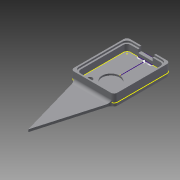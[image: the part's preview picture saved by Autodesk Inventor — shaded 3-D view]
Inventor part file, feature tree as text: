
AUTODESK INVENTOR PART (.ipt)
format: ipt  version: 2015 SP1 (Build 190203100, 203)  size: 185,856 bytes
history: native  units: mm
features: sketch x7, extrude x5, fillet x4, other x2, projected_geometry x1, reference x1
ambient origin geometry x8: Origin, YZ Plane, XZ Plane, XY Plane, X Axis, Y Axis, Z Axis, Center Point
bodies: Body1 (feature_tree)
feature tree (20):
  other  "Sólido1"
  extrude  "Extrusión1"  Depth=35.0mm
  sketch  "Boceto2"  dims[d2=6.0mm d3=6.0mm d4=3.0mm]
  extrude  "Extrusión2"  Depth=6.0mm
  fillet  "Empalme1"  Radius=3.0mm
  sketch  "Boceto4"  dims[d12=9.0mm d15=40.0mm]
  extrude  "Extrusión4"  Depth=23.0mm
  fillet  "Empalme2"  Radius=31.0mm
  fillet  "Empalme3"  Radius=5.0mm
  fillet  "Empalme4"  Radius=2.0mm
  other  "Labio1"
  extrude  "Extrusión5"  Depth=9.0mm
  extrude  "Extrusión6"  Depth=2.0mm
  sketch  "Boceto1"  dims[d0=27.0mm d1=35.0mm]
  sketch  "Boceto3"  dims[d5=2.0mm d6=0.0mm d7=23.0mm d8=31.0mm d9=5.0mm d10=0.0mm d11=2.0mm]
  sketch  "Boceto5"  dims[d16=1.5mm d17=0.0mm d18=2.0mm]
  projected_geometry  "Contorno proyectado1"
  sketch  "Boceto7"  dims[d19=2.0mm]
  sketch  "Boceto8"  dims[d20=2.0mm d21=1.0mm d22=1.0mm d23=0.0mm d24=0.0mm d25=0.0mm d26=0.0mm d27=2.0mm d28=4.0mm d29=0.0mm d30=0.0mm d31=1.0mm d32=0.0mm]
  reference  "Referencia2"
